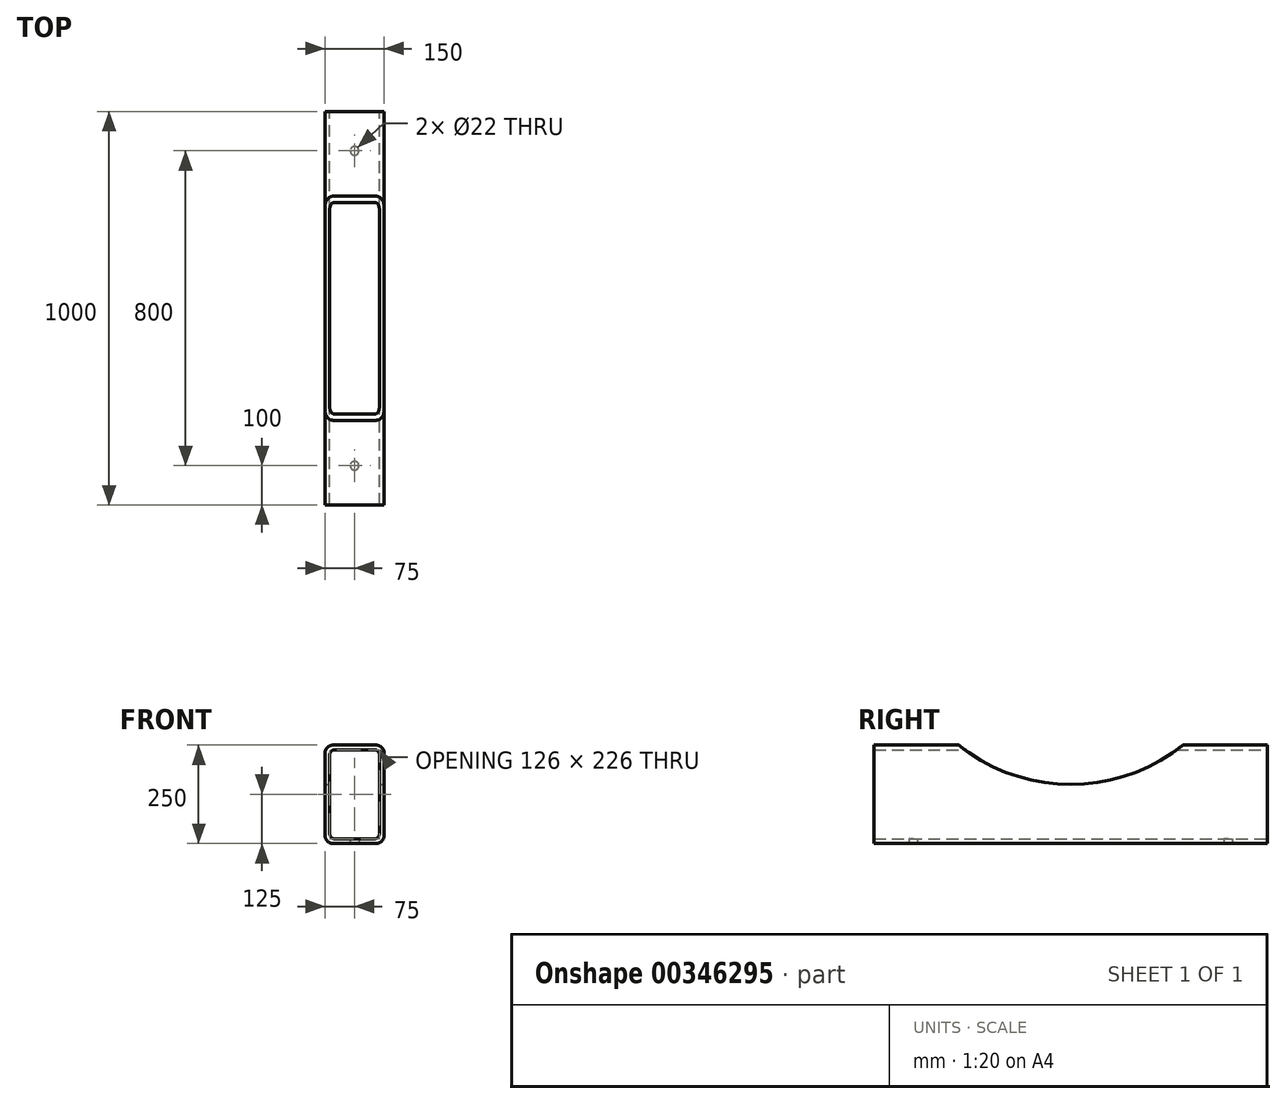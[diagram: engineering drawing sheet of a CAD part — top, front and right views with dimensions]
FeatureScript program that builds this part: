
annotation { "Feature Type Name" : "Feature", "Feature Type Description" : "" }
export const myFeature = defineFeature(function(context is Context, id is Id, definition is map)
    precondition{}
    {
        {
            var Q0;
            Q0=qCreatedBy(makeId("Front.planeOp"),FACE);
            var sketch = newSketch(context, id + "F0", { "sketchPlane" : qUnion([Q0])});
            skLineSegment(sketch, "E0", {"start": v(-480, -589) * mm, "end": v(-370, -589) * mm});
            skLineSegment(sketch, "E1", {"start": v(-500, -569) * mm, "end": v(-500, -359) * mm});
            skLineSegment(sketch, "E2", {"start": v(-350, -569) * mm, "end": v(-350, -359) * mm});
            skLineSegment(sketch, "E3", {"start": v(-480, -339) * mm, "end": v(-370, -339) * mm});
            skPoint(sketch, "E4.visualSharp", {"position": v(-350, -339) * mm});
            skArc(sketch, "E4.filletArc", {"start": v(-350, -359) * mm, "mid": v(-355.86, -344.86) * mm, "end": v(-370, -339) * mm});
            skPoint(sketch, "E5.visualSharp", {"position": v(-500, -339) * mm});
            skArc(sketch, "E5.filletArc", {"start": v(-480, -339) * mm, "mid": v(-494.14, -344.86) * mm, "end": v(-500, -359) * mm});
            skPoint(sketch, "E6.visualSharp", {"position": v(-500, -589) * mm});
            skArc(sketch, "E6.filletArc", {"start": v(-500, -569) * mm, "mid": v(-494.14, -583.14) * mm, "end": v(-480, -589) * mm});
            skPoint(sketch, "E7.visualSharp", {"position": v(-350, -589) * mm});
            skArc(sketch, "E7.filletArc", {"start": v(-370, -589) * mm, "mid": v(-355.86, -583.14) * mm, "end": v(-350, -569) * mm});
            skLineSegment(sketch, "E8.0", {"start": v(-476, -351) * mm, "end": v(-374, -351) * mm});
            skLineSegment(sketch, "E8.1", {"start": v(-488, -565) * mm, "end": v(-488, -363) * mm});
            skLineSegment(sketch, "E8.2", {"start": v(-476, -577) * mm, "end": v(-374, -577) * mm});
            skLineSegment(sketch, "E8.3", {"start": v(-362, -565) * mm, "end": v(-362, -363) * mm});
            skPoint(sketch, "E9.visualSharp", {"position": v(-362, -351) * mm});
            skArc(sketch, "E9.filletArc", {"start": v(-362, -363) * mm, "mid": v(-365.51, -354.51) * mm, "end": v(-374, -351) * mm});
            skPoint(sketch, "E10.visualSharp", {"position": v(-488, -351) * mm});
            skArc(sketch, "E10.filletArc", {"start": v(-476, -351) * mm, "mid": v(-484.49, -354.51) * mm, "end": v(-488, -363) * mm});
            skPoint(sketch, "E11.visualSharp", {"position": v(-362, -577) * mm});
            skArc(sketch, "E11.filletArc", {"start": v(-374, -577) * mm, "mid": v(-365.51, -573.49) * mm, "end": v(-362, -565) * mm});
            skPoint(sketch, "E12.visualSharp", {"position": v(-488, -577) * mm});
            skArc(sketch, "E12.filletArc", {"start": v(-488, -565) * mm, "mid": v(-484.49, -573.49) * mm, "end": v(-476, -577) * mm});
            skSolve(sketch);
        }
        {
            var Q0;
            Q0 = qSketchRegion(id + "F0", true);
            extrude(context, id + "F1", {"entities" : qUnion([Q0]), "depth" : 1000 * mm});
        }
        {
            var Q0;
            Q0=makeQuery(id+"F1.opExtrude","SWEPT_FACE",FACE,{"disambiguationData":[OSD([sQuery(id+"F0.wireOp",EDGE,"E0")])]});
            var sketch = newSketch(context, id + "F2", { "sketchPlane" : qUnion([Q0])});
            skLineSegment(sketch, "E13", {"start": v(-370, 500) * mm, "end": v(-480, 500) * mm});
            skLineSegment(sketch, "E14", {"start": v(-425, 500) * mm, "end": v(-425, 900) * mm});
            skCircle(sketch, "E15", {"center": v(-425, 900) * mm, "radius": 11 * mm});
            skCircle(sketch, "E16.MirrorC", {"center": v(-425, 100) * mm, "radius": 11 * mm});
            skSolve(sketch);
        }
        {
            var Q0;
            Q0 = qSketchRegion(id + "F2", true);
            extrude(context, id + "F3", {"entities" : qUnion([Q0]), "operationType" : NewBodyOperationType.REMOVE, "oppositeDirection" : true, "depth" : 25 * mm});
        }
        {
            var Q0;
            Q0=makeQuery(id+"F1.opExtrude","SWEPT_FACE",FACE,{"disambiguationData":[OSD([sQuery(id+"F0.wireOp",EDGE,"E2")])]});
            var sketch = newSketch(context, id + "F4", { "sketchPlane" : qUnion([Q0])});
            skPoint(sketch, "E17.startSnap0", {"position": v(-500, -359) * mm});
            skLineSegment(sketch, "E18", {"start": v(0, -359) * mm, "end": v(-1000, -359) * mm});
            skCircle(sketch, "E19", {"center": v(-500, 16) * mm, "radius": 455 * mm});
            skLineSegment(sketch, "E20", {"start": v(0, -464) * mm, "end": v(-1000, -464) * mm});
            skLineSegment(sketch, "E21.0", {"start": v(0, -339) * mm, "end": v(-1000, -339) * mm});
            skLineSegment(sketch, "E22", {"start": v(-500, -339) * mm, "end": v(-500, -439) * mm});
            skSolve(sketch);
        }
        {
            var Q0;
            Q0 = qSketchRegion(id + "F4", true);
            extrude(context, id + "F5", {"entities" : qUnion([Q0]), "operationType" : NewBodyOperationType.REMOVE, "oppositeDirection" : true, "depth" : 345 * mm});
        }
    });
